# Revit family: SLLED4HTMOWT40-50120-277V
name_source: partatom
category: Lighting Fixtures
revit_build: Autodesk Revit LT 2016 (Build: 20151007_0715(x64)
units: mm (PartAtom-declared; Revit-internal decimal feet)

## family parameters
Cut with Voids When Loaded = No
Host = Face
Light Source = Yes
Part Type = Normal
Room Calculation Point = No
Round Connector Dimension = Use Diameter
Shared = No

## types (2) — shared parameters
Color Filter = 16777215
Default Elevation = 4' - 0"
Description = STRIPLED offers both 4ft and 8ft configurations, color temperature 4000K & 5000K, with multiple mounting options.
Dimming Lamp Color Temperature Shift = <None>
Emit from Line Length = 2' - 0"
HOUSING MATERIAL = HOUSING MATERIAL
L = 3' - 11 3/16"
L1 = 1' - 11 19/32"
Lamp = LED
Manufacturer = BEGHELLI
Model = SLLED4HTMOWT50120-277V
Photometric Web File = SLLED4HTMOWT50120-277V.ies
REFLECTOR MATERIAL = REFLECTOR MATERIAL
TOTAL L = 4' - 0"
Tilt Angle = -90.00°
Type Comments = STRIPLED the ideal linear LED solution for budget conscious installations or replacement of linear fluorescent luminaires which are typically used in warehouses, aisle lighting, service corridors, office, garages, retail and other commercial environments. STRIPLED is IP44 and DLC qualified for utility rebates.
Type Image = STRIP LED PICTURE.PNG

## per-type parameters (varying)
| type | Wattage Comments |
| SLLED4HTMOWT40-50120-277V | 38.3W |
| SLLED4HTMOWT50-50120-277V | 41.6W |

## geometry (parser evidence)
native form markers: Sweep x9
no freeform markers — native parametric forms only
